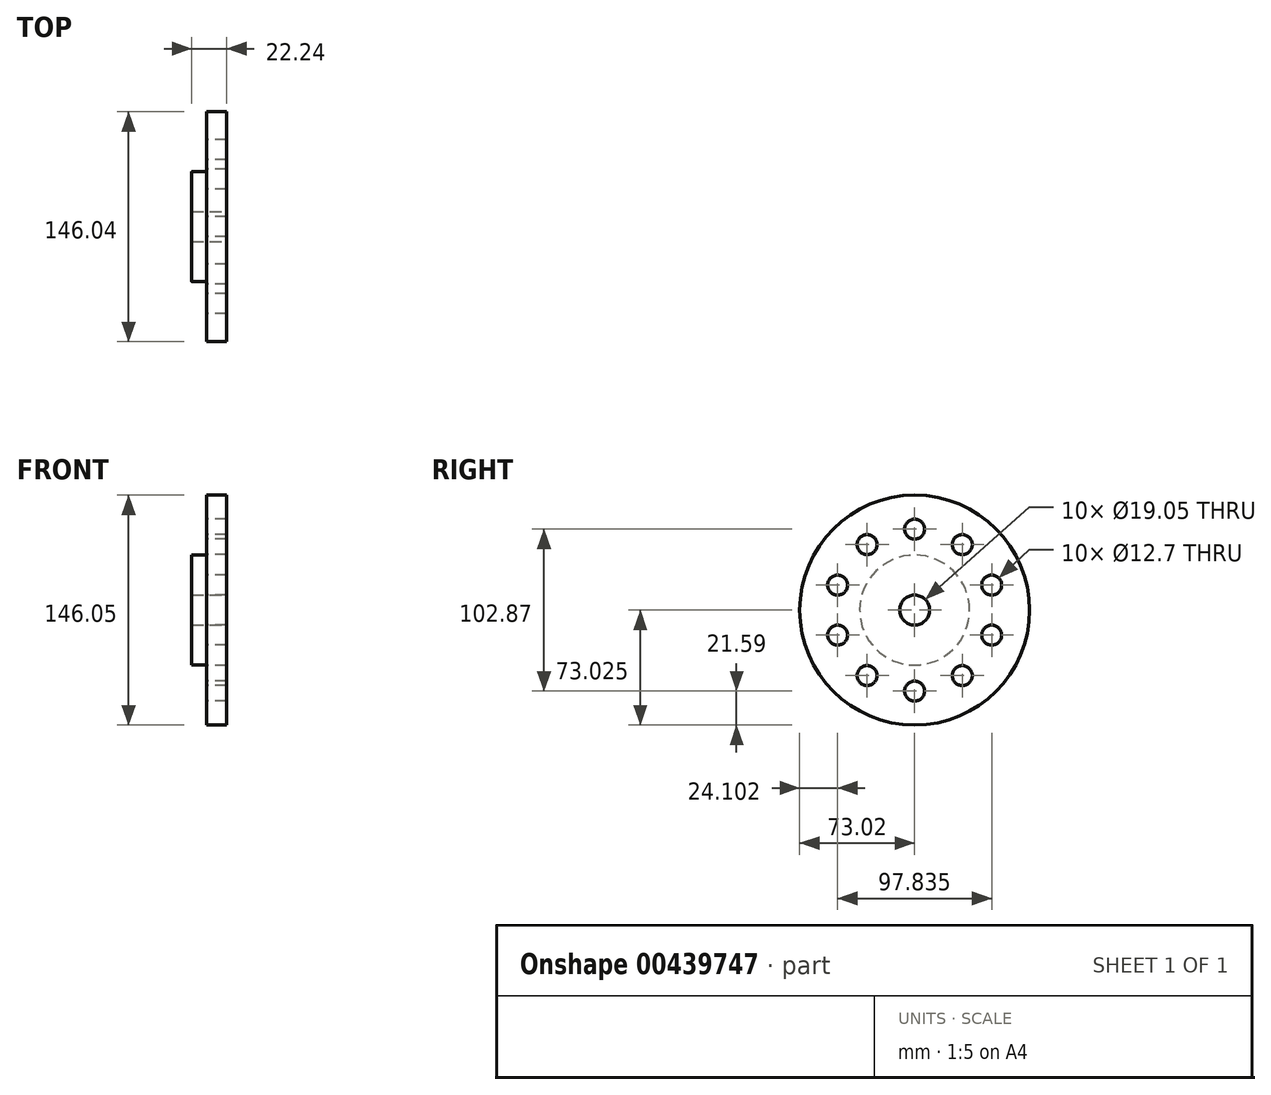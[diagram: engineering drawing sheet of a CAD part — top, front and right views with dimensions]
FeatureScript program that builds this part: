
annotation { "Feature Type Name" : "Feature", "Feature Type Description" : "" }
export const myFeature = defineFeature(function(context is Context, id is Id, definition is map)
    precondition{}
    {
        {
            var Q0;
            Q0=qCreatedBy(makeId("Front.planeOp"),FACE);
            var sketch = newSketch(context, id + "F0", { "sketchPlane" : qUnion([Q0])});
            skLineSegment(sketch, "E0", {"start": v(0, 0) * mm, "end": v(25.4, 0) * mm});
            skLineSegment(sketch, "E1", {"start": v(0, 0) * mm, "end": v(0, 25.4) * mm});
            skLineSegment(sketch, "E2", {"start": v(0, 25.4) * mm, "end": v(9.54, 25.4) * mm});
            skLineSegment(sketch, "E3", {"start": v(9.54, 25.4) * mm, "end": v(9.54, 63.5) * mm});
            skLineSegment(sketch, "E4", {"start": v(9.54, 63.5) * mm, "end": v(22.24, 63.5) * mm});
            skLineSegment(sketch, "E5", {"start": v(22.24, 63.5) * mm, "end": v(22.24, 0) * mm});
            skLineSegment(sketch, "E6", {"start": v(22.24, 0) * mm, "end": v(22.24, -9.52) * mm});
            skLineSegment(sketch, "E7", {"start": v(22.24, -9.52) * mm, "end": v(-25.58, -9.52) * mm});
            skSolve(sketch);
        }
        {
            var Q0;
            {var subQ0=sQuery(id+"F0.wireOp",EDGE,"E1");Q0=makeQuery(id+"F0.imprint","IMPRINT",FACE,{"disambiguationData":[TD([[makeQuery(id+"F0.imprint","IMPRINT",EDGE,{"derivedFrom":subQ0}),-1.0]])]});}
            var Q1;
            Q1=sQuery(id+"F0.wireOp",EDGE,"E7");
            revolve(context, id + "F1", {"entities" : qUnion([Q0]), "axis" : qUnion([Q1]), "revolveType" : RevolveType.FULL});
        }
        {
            var Q0;
            Q0=makeQuery(id+"F1.opRevolve","SWEPT_FACE",FACE,{"disambiguationData":[OSD([sQuery(id+"F0.wireOp",EDGE,"E1")])]});
            var sketch = newSketch(context, id + "F2", { "sketchPlane" : qUnion([Q0])});
            skLineSegment(sketch, "E8", {"start": v(0, 0) * mm, "end": v(0, 41.91) * mm});
            skPoint(sketch, "E9", {"position": v(0, 41.91) * mm});
            skSolve(sketch);
        }
        {
            var Q0;
            Q0=sQuery(id+"F2.wireOp",VERTEX,"E9");
            var Q1;
            Q1=makeQuery(id+"F1.opRevolve","SWEPT_BODY",BODY,{"disambiguationData":[OSD([sQuery(id+"F0.wireOp",EDGE,"E0"),sQuery(id+"F0.wireOp",EDGE,"E1"),sQuery(id+"F0.wireOp",EDGE,"E2"),sQuery(id+"F0.wireOp",EDGE,"E3"),sQuery(id+"F0.wireOp",EDGE,"E4"),sQuery(id+"F0.wireOp",EDGE,"E5")])]});
            hole(context, id + "F3", {"style" : HoleStyle.SIMPLE, "endStyle" : HoleEndStyle.THROUGH, "holeDiameter" : 12.7 * mm, "isTappedThrough" : true, "tappedDepth" : 12.7 * mm, "tapClearance" : 3, "locations" : qUnion([Q0]), "scope" : qUnion([Q1])});
        }
        {
            var Q0;
            Q0=makeQuery(id+"F1.opRevolve","SWEPT_BODY",BODY,{"disambiguationData":[OSD([sQuery(id+"F0.wireOp",EDGE,"E0"),sQuery(id+"F0.wireOp",EDGE,"E1"),sQuery(id+"F0.wireOp",EDGE,"E2"),sQuery(id+"F0.wireOp",EDGE,"E3"),sQuery(id+"F0.wireOp",EDGE,"E4"),sQuery(id+"F0.wireOp",EDGE,"E5")])]});
            var Q1;
            Q1=makeQuery(id+"F1.opRevolve","SWEPT_EDGE",EDGE,{"disambiguationData":[OSD([sQuery(id+"F0.wireOp",EDGE,"E0"),sQuery(id+"F0.wireOp",EDGE,"E1")])]});
            circularPattern(context, id + "F4", {"entities" : qUnion([Q0]), "axis" : qUnion([Q1]), "angle" : 360 * degree, "instanceCount" : 10, "equalSpace" : true});
        }
    });
